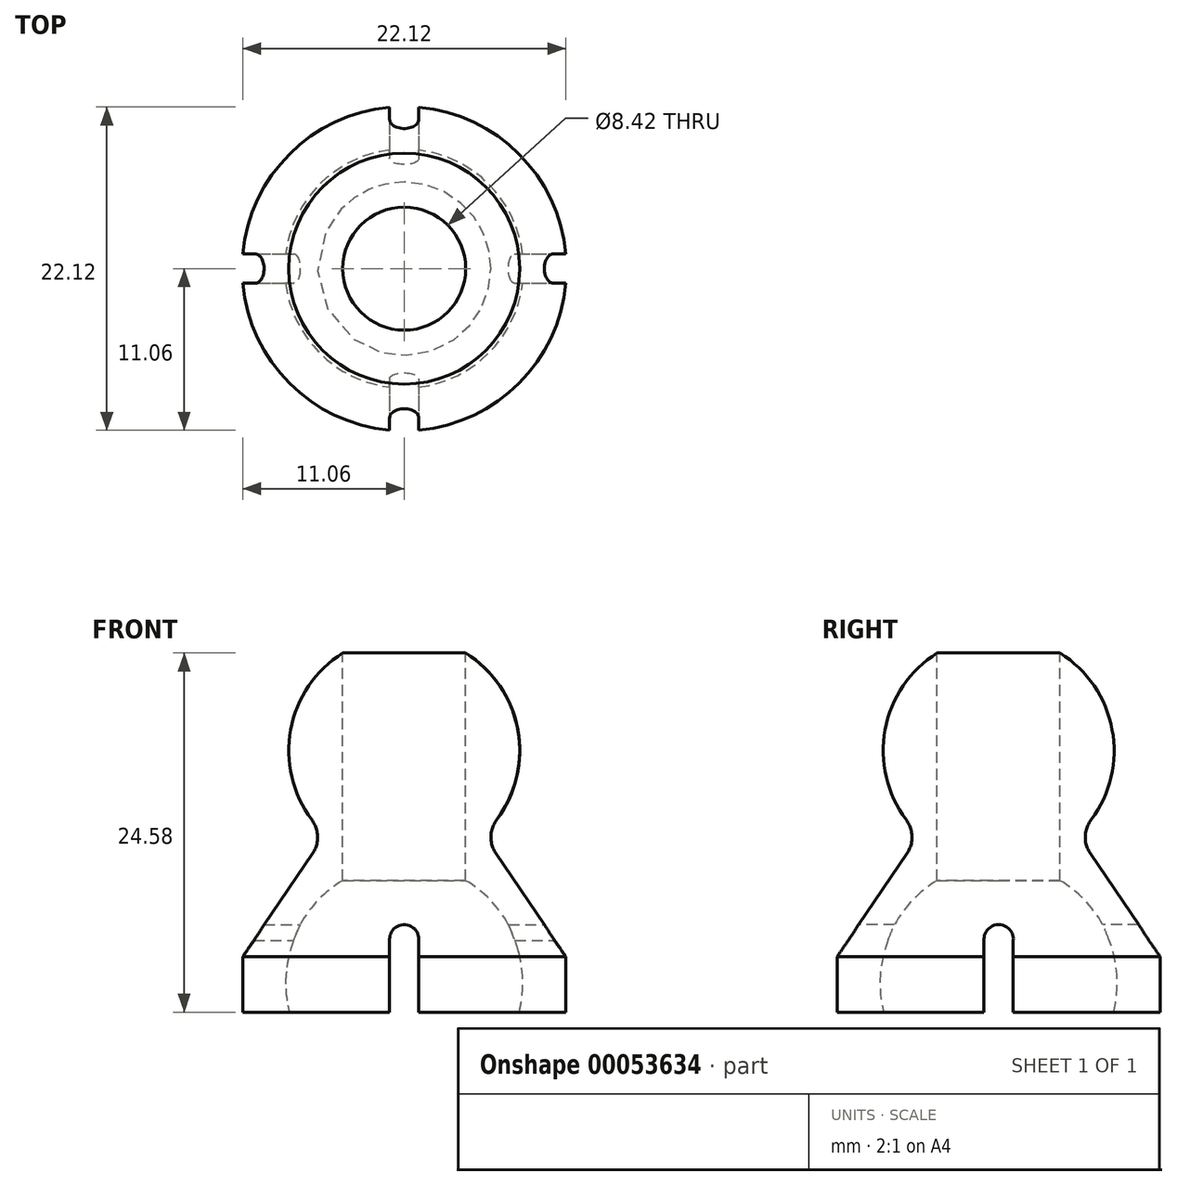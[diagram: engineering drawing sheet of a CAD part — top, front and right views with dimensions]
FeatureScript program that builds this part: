
annotation { "Feature Type Name" : "Feature", "Feature Type Description" : "" }
export const myFeature = defineFeature(function(context is Context, id is Id, definition is map)
    precondition{}
    {
        {
            var Q0;
            Q0=qCreatedBy(makeId("Front.planeOp"),FACE);
            var sketch = newSketch(context, id + "F0", { "sketchPlane" : qUnion([Q0])});
            skArc(sketch, "E0", {"start": v(0, 4.19) * mm, "mid": v(0.6, 4.2) * mm, "end": v(1.18, 4.27) * mm});
            skLineSegment(sketch, "E1", {"start": v(6.28, 5.03) * mm, "end": v(11.1, -2.02) * mm});
            skLineSegment(sketch, "E2", {"start": v(11.1, -2.02) * mm, "end": v(11.1, -5.81) * mm});
            skLineSegment(sketch, "E3", {"start": v(11.1, -5.81) * mm, "end": v(7.93, -5.81) * mm});
            skArc(sketch, "E4", {"start": v(7.93, -5.81) * mm, "mid": v(6.8, 0.73) * mm, "end": v(1.18, 4.27) * mm});
            skLineSegment(sketch, "E5", {"start": v(0, 10.09) * mm, "end": v(7.64, 10.09) * mm, "construction": true});
            skPoint(sketch, "E6", {"position": v(0, 19.99) * mm});
            skPoint(sketch, "E7", {"position": v(0, 10.09) * mm});
            skPoint(sketch, "E8.orphan", {"position": v(-7.64, 10.09) * mm});
            skPoint(sketch, "E9.orphan", {"position": v(0, -5.81) * mm});
            skLineSegment(sketch, "E10", {"start": v(0, 19.99) * mm, "end": v(0, 4.19) * mm});
            skArc(sketch, "E11.trimOffspring", {"start": v(6.33, 7.35) * mm, "mid": v(7.06, 15.62) * mm, "end": v(0, 19.99) * mm});
            skLineSegment(sketch, "E12", {"start": v(0, 4.19) * mm, "end": v(0, -5.81) * mm, "construction": true});
            skPoint(sketch, "E13.visualSharp", {"position": v(5.4, 6.32) * mm});
            skArc(sketch, "E13.filletArc", {"start": v(6.33, 7.35) * mm, "mid": v(5.93, 6.2) * mm, "end": v(6.28, 5.03) * mm});
            skSolve(sketch);
        }
        {
            var Q0;
            Q0 = qSketchRegion(id + "F0", true);
            var Q1;
            Q1=sQuery(id+"F0.wireOp",EDGE,"E12");
            revolve(context, id + "F1", {"entities" : qUnion([Q0]), "axis" : qUnion([Q1]), "revolveType" : RevolveType.FULL});
        }
        {
            var Q0;
            Q0=qCreatedBy(makeId("Top.planeOp"),FACE);
            var sketch = newSketch(context, id + "F2", { "sketchPlane" : qUnion([Q0])});
            skCircle(sketch, "E14", {"center": v(0, 0) * mm, "radius": 4.2 * mm});
            skSolve(sketch);
        }
        {
            var Q0;
            Q0 = qSketchRegion(id + "F2", true);
            extrude(context, id + "F3", {"entities" : qUnion([Q0]), "operationType" : NewBodyOperationType.REMOVE, "endBound" : BoundingType.SYMMETRIC, "oppositeDirection" : true, "depth" : 50 * mm});
        }
        {
            var Q0;
            Q0=qCreatedBy(makeId("Right.planeOp"),FACE);
            var sketch = newSketch(context, id + "F4", { "sketchPlane" : qUnion([Q0])});
            skLineSegment(sketch, "E15.bottom", {"start": v(1, -5.81) * mm, "end": v(-1, -5.81) * mm});
            skLineSegment(sketch, "E15.left", {"start": v(1, -5.81) * mm, "end": v(1, -0.91) * mm});
            skLineSegment(sketch, "E15.right", {"start": v(-1, -5.81) * mm, "end": v(-1, -0.81) * mm});
            skArc(sketch, "E16", {"start": v(1, -0.91) * mm, "mid": v(0.05, 0.19) * mm, "end": v(-1, -0.81) * mm});
            skSolve(sketch);
        }
        {
            var Q0;
            Q0 = qSketchRegion(id + "F4", true);
            extrude(context, id + "F5", {"entities" : qUnion([Q0]), "operationType" : NewBodyOperationType.REMOVE, "endBound" : BoundingType.SYMMETRIC, "oppositeDirection" : true, "depth" : 25 * mm});
        }
        {
            var Q0;
            Q0=qCreatedBy(makeId("Front.planeOp"),FACE);
            var sketch = newSketch(context, id + "F6", { "sketchPlane" : qUnion([Q0])});
            skLineSegment(sketch, "E17", {"start": v(-1, -5.81) * mm, "end": v(-1, -0.81) * mm});
            skLineSegment(sketch, "E18", {"start": v(1, -5.81) * mm, "end": v(1, -0.81) * mm});
            skArc(sketch, "E19", {"start": v(1, -0.81) * mm, "mid": v(0, 0.19) * mm, "end": v(-1, -0.81) * mm});
            skLineSegment(sketch, "E20", {"start": v(-1, -5.81) * mm, "end": v(1, -5.81) * mm});
            skSolve(sketch);
        }
        {
            var Q0;
            Q0 = qSketchRegion(id + "F6", true);
            extrude(context, id + "F7", {"entities" : qUnion([Q0]), "operationType" : NewBodyOperationType.REMOVE, "endBound" : BoundingType.SYMMETRIC, "oppositeDirection" : true, "depth" : 25 * mm});
        }
    });
